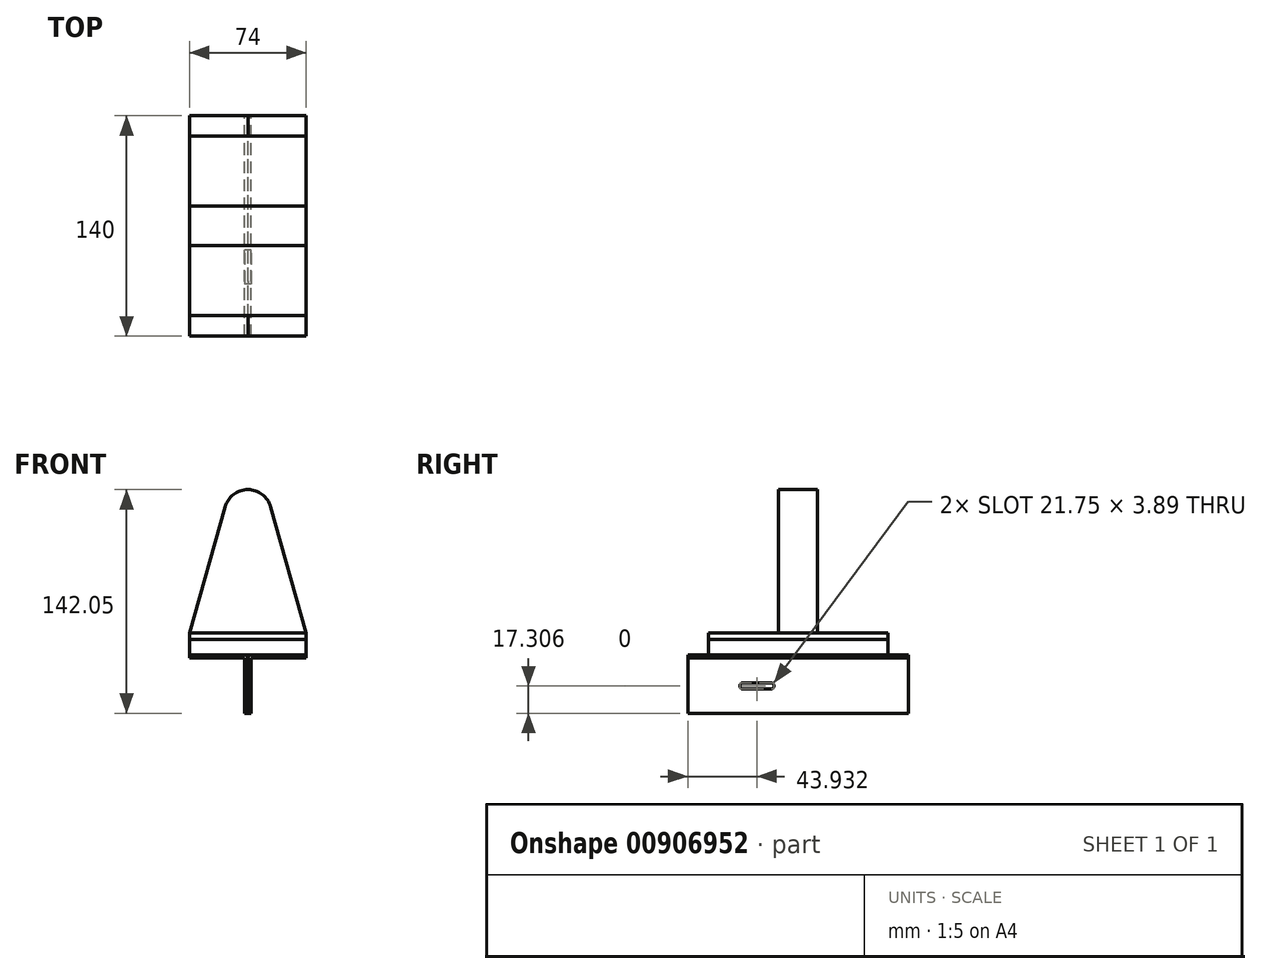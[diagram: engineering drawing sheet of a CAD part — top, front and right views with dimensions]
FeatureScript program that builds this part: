
annotation { "Feature Type Name" : "Feature", "Feature Type Description" : "" }
export const myFeature = defineFeature(function(context is Context, id is Id, definition is map)
    precondition{}
    {
        {
            var Q0;
            Q0=qCreatedBy(makeId("Top.planeOp"),FACE);
            var sketch = newSketch(context, id + "F0", { "sketchPlane" : qUnion([Q0])});
            skLineSegment(sketch, "E0.bottom", {"start": v(37, 57) * mm, "end": v(-37, 57) * mm});
            skLineSegment(sketch, "E0.top", {"start": v(37, -57) * mm, "end": v(-37, -57) * mm});
            skLineSegment(sketch, "E0.left", {"start": v(37, 57) * mm, "end": v(37, -57) * mm});
            skLineSegment(sketch, "E0.right", {"start": v(-37, 57) * mm, "end": v(-37, -57) * mm});
            skPoint(sketch, "E0.middle", {"position": v(0, 0) * mm});
            skSolve(sketch);
        }
        {
            var Q0;
            Q0=makeQuery(id+"F0.imprint","IMPRINT",FACE,{"disambiguationData":[TD([[makeQuery(id+"F0.imprint","IMPRINT",EDGE,{"derivedFrom":sQuery(id+"F0.wireOp",EDGE,"E0.bottom")}),1.0]])]});
            extrude(context, id + "F1", {"entities" : qUnion([Q0]), "depth" : 10 * mm, "offsetDistance" : 25 * mm});
        }
        {
            var Q0;
            Q0=qCreatedBy(makeId("Front.planeOp"),FACE);
            var sketch = newSketch(context, id + "F2", { "sketchPlane" : qUnion([Q0])});
            skLineSegment(sketch, "E1.bottom", {"start": v(2.5, 0) * mm, "end": v(37, 0) * mm});
            skLineSegment(sketch, "E1.left", {"start": v(0, -2.5) * mm, "end": v(0, -37) * mm});
            skLineSegment(sketch, "E1.right", {"start": v(37, 0) * mm, "end": v(37, -2) * mm});
            skLineSegment(sketch, "E2.top", {"start": v(37, -2) * mm, "end": v(2, -2) * mm});
            skLineSegment(sketch, "E2.right", {"start": v(2, -37) * mm, "end": v(2, -2) * mm});
            skLineSegment(sketch, "E3", {"start": v(2, -37) * mm, "end": v(0, -37) * mm});
            skPoint(sketch, "E4.visualSharp", {"position": v(0, 0) * mm});
            skArc(sketch, "E4.filletArc", {"start": v(2.5, 0) * mm, "mid": v(0.73, -0.73) * mm, "end": v(0, -2.5) * mm});
            skSolve(sketch);
        }
        {
            var Q0;
            Q0 = qSketchRegion(id + "F2", true);
            extrude(context, id + "F3", {"entities" : qUnion([Q0]), "endBound" : BoundingType.SYMMETRIC, "depth" : 140 * mm, "offsetDistance" : 25 * mm});
        }
        {
            var Q0;
            Q0=makeQuery(id+"F3.opExtrude","SWEPT_BODY",BODY,{"disambiguationData":[OSD([sQuery(id+"F2.wireOp",EDGE,"E1.bottom"),sQuery(id+"F2.wireOp",EDGE,"E1.left"),sQuery(id+"F2.wireOp",EDGE,"E1.right"),sQuery(id+"F2.wireOp",EDGE,"E2.top"),sQuery(id+"F2.wireOp",EDGE,"E2.right"),sQuery(id+"F2.wireOp",EDGE,"E3"),sQuery(id+"F2.wireOp",EDGE,"E4.filletArc")])]});
            var Q1;
            Q1=qCreatedBy(makeId("Right.planeOp"),FACE);
            mirror(context, id + "F4", {"entities" : qUnion([Q0]), "mirrorPlane" : qUnion([Q1])});
        }
        {
            var Q0;
            Q0=makeQuery(id+"F1.opExtrude","CAP_FACE",FACE,{"disambiguationData":[OSD([sQuery(id+"F0.wireOp",EDGE,"E0.bottom"),sQuery(id+"F0.wireOp",EDGE,"E0.top"),sQuery(id+"F0.wireOp",EDGE,"E0.left"),sQuery(id+"F0.wireOp",EDGE,"E0.right")])],"isStart":false});
            var sketch = newSketch(context, id + "F5", { "sketchPlane" : qUnion([Q0])});
            skLineSegment(sketch, "E5.0.0", {"start": v(-37, -57) * mm, "end": v(37, -57) * mm});
            skLineSegment(sketch, "E5.0.1", {"start": v(37, -57) * mm, "end": v(37, 57) * mm});
            skLineSegment(sketch, "E5.0.2", {"start": v(37, 57) * mm, "end": v(-37, 57) * mm});
            skLineSegment(sketch, "E5.0.3", {"start": v(-37, 57) * mm, "end": v(-37, -57) * mm});
            skSolve(sketch);
        }
        {
            var Q0;
            Q0 = qSketchRegion(id + "F5", true);
            extrude(context, id + "F6", {"entities" : qUnion([Q0]), "depth" : 4 * mm, "offsetDistance" : 25 * mm});
        }
        {
            var Q0;
            Q0=qCreatedBy(makeId("Front.planeOp"),FACE);
            var sketch = newSketch(context, id + "F7", { "sketchPlane" : qUnion([Q0])});
            skLineSegment(sketch, "E6", {"start": v(-37, 14) * mm, "end": v(-14.44, 94.11) * mm});
            skLineSegment(sketch, "E7", {"start": v(14.44, 94.11) * mm, "end": v(37, 14) * mm});
            skLineSegment(sketch, "E8", {"start": v(37, 14) * mm, "end": v(-37, 14) * mm});
            skPoint(sketch, "E9.visualSharp", {"position": v(0, 145.38) * mm});
            skArc(sketch, "E9.filletArc", {"start": v(14.44, 94.11) * mm, "mid": v(0, 105.05) * mm, "end": v(-14.44, 94.11) * mm});
            skSolve(sketch);
        }
        {
            var Q0;
            Q0=makeQuery(id+"F7.imprint","IMPRINT",FACE,{"disambiguationData":[TD([[makeQuery(id+"F7.imprint","IMPRINT",EDGE,{"derivedFrom":sQuery(id+"F7.wireOp",EDGE,"E6")}),-1.0]])]});
            extrude(context, id + "F8", {"entities" : qUnion([Q0]), "operationType" : NewBodyOperationType.ADD, "endBound" : BoundingType.SYMMETRIC, "depth" : 25 * mm, "offsetDistance" : 25 * mm});
        }
        {
            var Q0;
            Q0=makeQuery(id+"F4.opPattern","COPY",FACE,{"derivedFrom":makeQuery(id+"F3.opExtrude","SWEPT_FACE",FACE,{"disambiguationData":[OSD([sQuery(id+"F2.wireOp",EDGE,"E2.right")])]}),"instanceName":"1"});
            var sketch = newSketch(context, id + "F9", { "sketchPlane" : qUnion([Q0])});
            skLineSegment(sketch, "E10.bottom", {"start": v(17.14, -21.64) * mm, "end": v(35, -21.64) * mm});
            skLineSegment(sketch, "E10.top", {"start": v(17.14, -17.75) * mm, "end": v(35, -17.75) * mm});
            skArc(sketch, "E11", {"start": v(35, -21.64) * mm, "mid": v(36.94, -19.7) * mm, "end": v(35, -17.75) * mm});
            skArc(sketch, "E12", {"start": v(17.14, -17.75) * mm, "mid": v(15.2, -19.7) * mm, "end": v(17.14, -21.64) * mm});
            skLineSegment(sketch, "E13", {"start": v(17.14, -17.75) * mm, "end": v(17.14, -21.64) * mm, "construction": true});
            skLineSegment(sketch, "E14", {"start": v(35, -17.75) * mm, "end": v(35, -21.64) * mm, "construction": true});
            skSolve(sketch);
        }
        {
            var Q0;
            Q0 = qSketchRegion(id + "F9", true);
            extrude(context, id + "F10", {"entities" : qUnion([Q0]), "operationType" : NewBodyOperationType.REMOVE, "endBound" : BoundingType.THROUGH_ALL, "oppositeDirection" : true, "depth" : 25 * mm, "offsetDistance" : 25 * mm});
        }
    });
